# Revit family: BC_Hitachi_CH-BOX-CH-AP-SSX_LOD200
name_source: partatom
category: Equipement de génie climatique
revit_build: Autodesk Revit 2015 (Build: 20140606_1530(x64)
units: mm (PartAtom-declared; Revit-internal decimal feet)

## types (2) — shared parameters
CALC_Refrigerant Gas Diameter = 30.88 mm  [stored 0.101312 ft]
CALC_Refrigerant Gas HL Left = 200 mm  [stored 0.656168 ft]
CALC_Refrigerant Gas L Left = 250 mm  [stored 0.82021 ft]
CALC_Refrigerant Gas Low Pressure Diameter = 26.55 mm  [stored 0.0871063 ft]
Description = Single CH-Box
Fabricant = Hitachi
Gas Diameter = 15.88 mm  [stored 0.0520997 ft]
Mass = 6.00 kg
Modèle = Single CH-Box
Nominal Voltage = 230 V
Overall Height = 191 mm  [stored 0.62664 ft]
Overall Width = 301 mm  [stored 0.987533 ft]
Rated Frequency (Hz) = 50
Refrigerant Gas Diameter = 15.88 mm  [stored 0.0520997 ft]
Refrigerant Gas Low Pressure Diameter = 19.05 mm  [stored 0.0625 ft]

## per-type parameters (varying)
| type | CALC_Refrigerant Gas Right | Material Box | Overall Depth | Product Code |
| CH-AP160SSX | 89 mm  [stored 0.291995 ft] | Par défaut | 214 mm  [stored 0.7021 ft] | 60292158 |
| CH-AP280SSX | 96 mm  [stored 0.314961 ft] | <Par catégorie> | 180 mm  [stored 0.590551 ft] | 60292159 |

note: column(s) folded — value = type name in every type: Commentaires du type

note: [stored X ft] marks values corroborated as IEEE doubles in the binary element streams (Revit-internal decimal feet)
